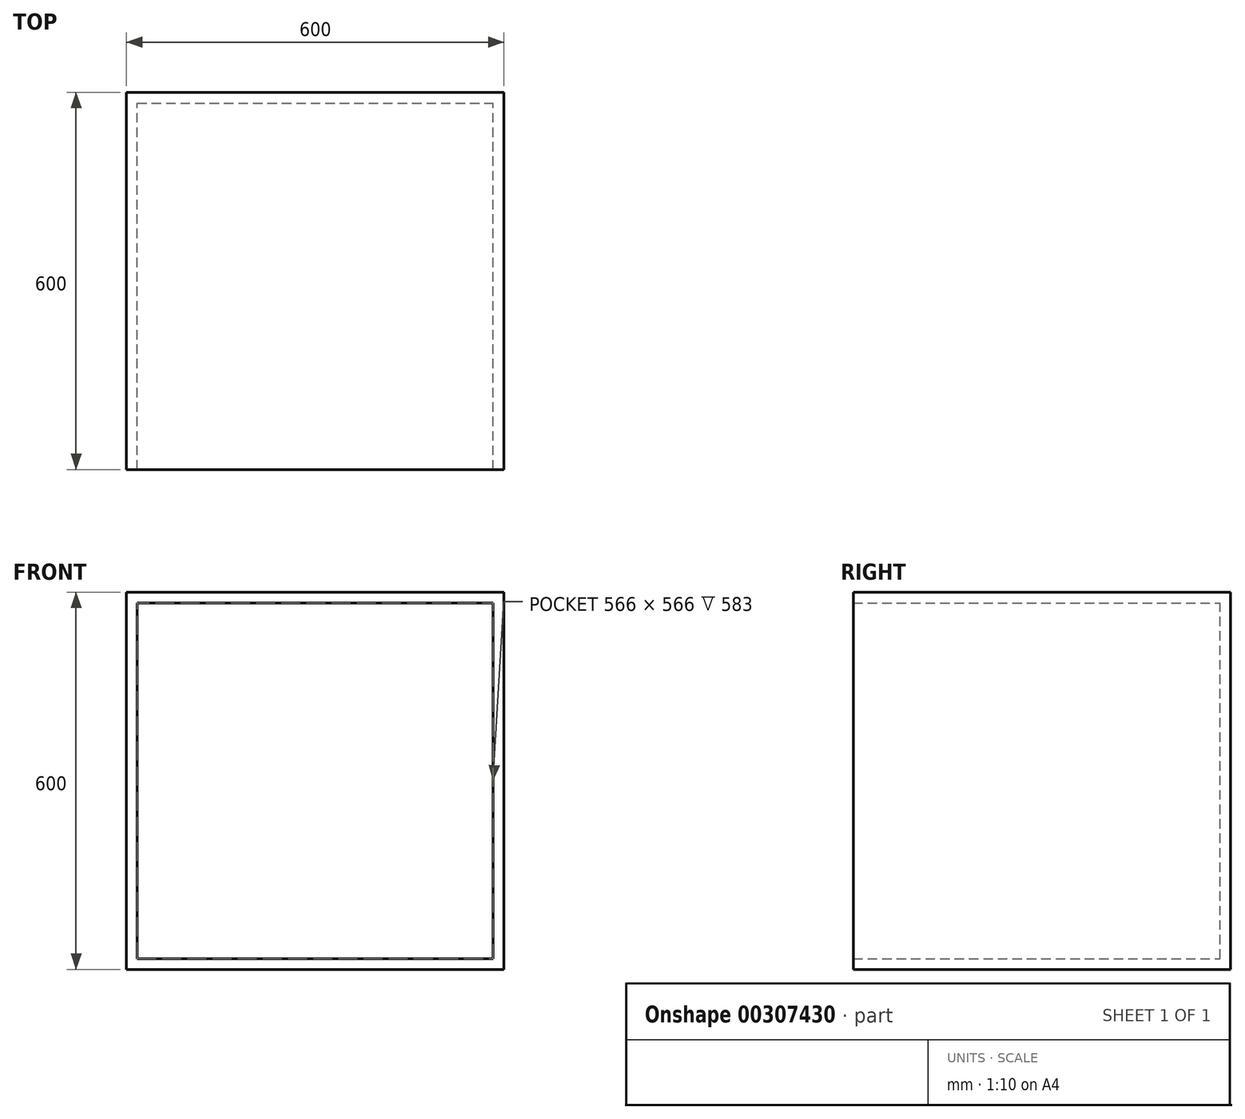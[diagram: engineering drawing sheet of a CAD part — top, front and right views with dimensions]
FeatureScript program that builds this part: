
annotation { "Feature Type Name" : "Feature", "Feature Type Description" : "" }
export const myFeature = defineFeature(function(context is Context, id is Id, definition is map)
    precondition{}
    {
        {
            var Q0;
            Q0=qCreatedBy(makeId("Front.planeOp"),FACE);
            var sketch = newSketch(context, id + "F0", { "sketchPlane" : qUnion([Q0])});
            skLineSegment(sketch, "E0.bottom", {"start": v(0, 0) * mm, "end": v(600, 0) * mm});
            skLineSegment(sketch, "E0.top", {"start": v(0, -600) * mm, "end": v(600, -600) * mm});
            skLineSegment(sketch, "E0.left", {"start": v(0, -600) * mm, "end": v(0, 0) * mm});
            skLineSegment(sketch, "E0.right", {"start": v(600, -600) * mm, "end": v(600, 0) * mm});
            skSolve(sketch);
        }
        {
            var Q0;
            Q0=makeQuery(id+"F0.imprint","IMPRINT",FACE,{"disambiguationData":[TD([[makeQuery(id+"F0.imprint","IMPRINT",EDGE,{"derivedFrom":sQuery(id+"F0.wireOp",EDGE,"E0.bottom")}),-1.0]])]});
            extrude(context, id + "F1", {"entities" : qUnion([Q0]), "depth" : 600 * mm, "offsetDistance" : 25 * mm});
        }
        {
            var Q0;
            Q0=makeQuery(id+"F1.opExtrude","CAP_FACE",FACE,{"disambiguationData":[OSD([sQuery(id+"F0.wireOp",EDGE,"E0.bottom"),sQuery(id+"F0.wireOp",EDGE,"E0.top"),sQuery(id+"F0.wireOp",EDGE,"E0.left"),sQuery(id+"F0.wireOp",EDGE,"E0.right")])],"isStart":false});
            shell(context, id + "F2", {"entities" : qUnion([Q0]), "thickness" : 17 * mm});
        }
    });
